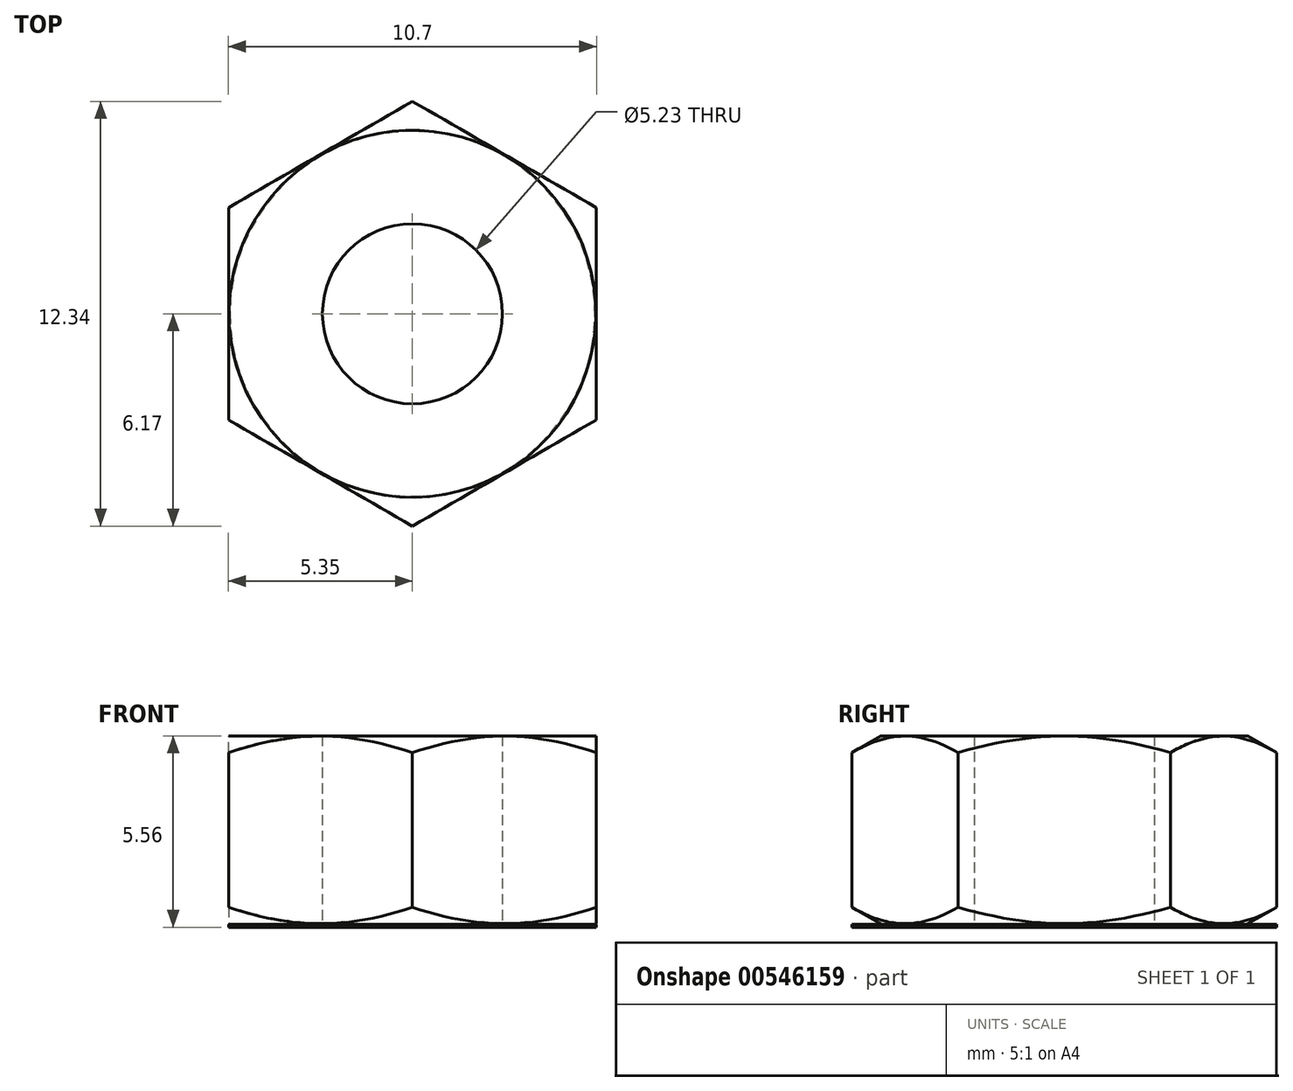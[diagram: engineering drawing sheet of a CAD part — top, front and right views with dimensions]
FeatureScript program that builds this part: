
annotation { "Feature Type Name" : "Feature", "Feature Type Description" : "" }
export const myFeature = defineFeature(function(context is Context, id is Id, definition is map)
    precondition{}
    {
        {
            var Q0;
            Q0=qCreatedBy(makeId("Top.planeOp"),FACE);
            var sketch = newSketch(context, id + "F0", { "sketchPlane" : qUnion([Q0])});
            skCircle(sketch, "E0.cCircle", {"center": v(0, 0) * mm, "radius": 5.35 * mm, "construction": true});
            skLineSegment(sketch, "E0.0", {"start": v(5.35, 3.09) * mm, "end": v(5.35, -3.09) * mm});
            skLineSegment(sketch, "E0.1", {"start": v(5.35, -3.09) * mm, "end": v(0, -6.17) * mm});
            skLineSegment(sketch, "E0.2", {"start": v(0, -6.17) * mm, "end": v(-5.35, -3.09) * mm});
            skLineSegment(sketch, "E0.3", {"start": v(-5.35, -3.09) * mm, "end": v(-5.35, 3.09) * mm});
            skLineSegment(sketch, "E0.4", {"start": v(-5.35, 3.09) * mm, "end": v(0, 6.17) * mm});
            skLineSegment(sketch, "E0.5", {"start": v(0, 6.17) * mm, "end": v(5.35, 3.09) * mm});
            skPoint(sketch, "E0.0.midPoint", {"position": v(5.35, 0) * mm});
            skCircle(sketch, "E1", {"center": v(0, 0) * mm, "radius": 2.62 * mm});
            skSolve(sketch);
        }
        {
            var Q0;
            Q0=makeQuery(id+"F0.imprint","IMPRINT",FACE,{"disambiguationData":[TD([[makeQuery(id+"F0.imprint","IMPRINT",EDGE,{"derivedFrom":sQuery(id+"F0.wireOp",EDGE,"E0.0")}),-1.0]])]});
            extrude(context, id + "F1", {"entities" : qUnion([Q0]), "depth" : 5.56 * mm, "offsetDistance" : 25.4 * mm});
        }
        {
            var Q0;
            Q0=qCreatedBy(makeId("Front.planeOp"),FACE);
            var sketch = newSketch(context, id + "F2", { "sketchPlane" : qUnion([Q0])});
            skLineSegment(sketch, "E2", {"start": v(0, 5.66) * mm, "end": v(0, 0) * mm, "construction": true});
            skLineSegment(sketch, "E3", {"start": v(0, 2.83) * mm, "end": v(5.38, 2.83) * mm, "construction": true});
            skLineSegment(sketch, "E4", {"start": v(5.3, 5.58) * mm, "end": v(8.2, 5.58) * mm});
            skLineSegment(sketch, "E5", {"start": v(8.2, 5.58) * mm, "end": v(8.2, 3.91) * mm});
            skLineSegment(sketch, "E6", {"start": v(8.2, 3.91) * mm, "end": v(5.3, 5.58) * mm});
            skLineSegment(sketch, "E7.MirrorCS", {"start": v(8.2, 0.08) * mm, "end": v(8.2, 1.75) * mm});
            skLineSegment(sketch, "E8.MirrorCS", {"start": v(5.3, 0.08) * mm, "end": v(8.2, 0.08) * mm});
            skLineSegment(sketch, "E9.MirrorCS", {"start": v(8.2, 1.75) * mm, "end": v(5.3, 0.08) * mm});
            skSolve(sketch);
        }
        {
            var Q0;
            Q0 = qSketchRegion(id + "F2", true);
            var Q1;
            Q1=sQuery(id+"F2.wireOp",EDGE,"E2");
            revolve(context, id + "F3", {"operationType" : NewBodyOperationType.REMOVE, "entities" : qUnion([Q0]), "axis" : qUnion([Q1]), "revolveType" : RevolveType.FULL, "oppositeDirection" : true});
        }
    });
